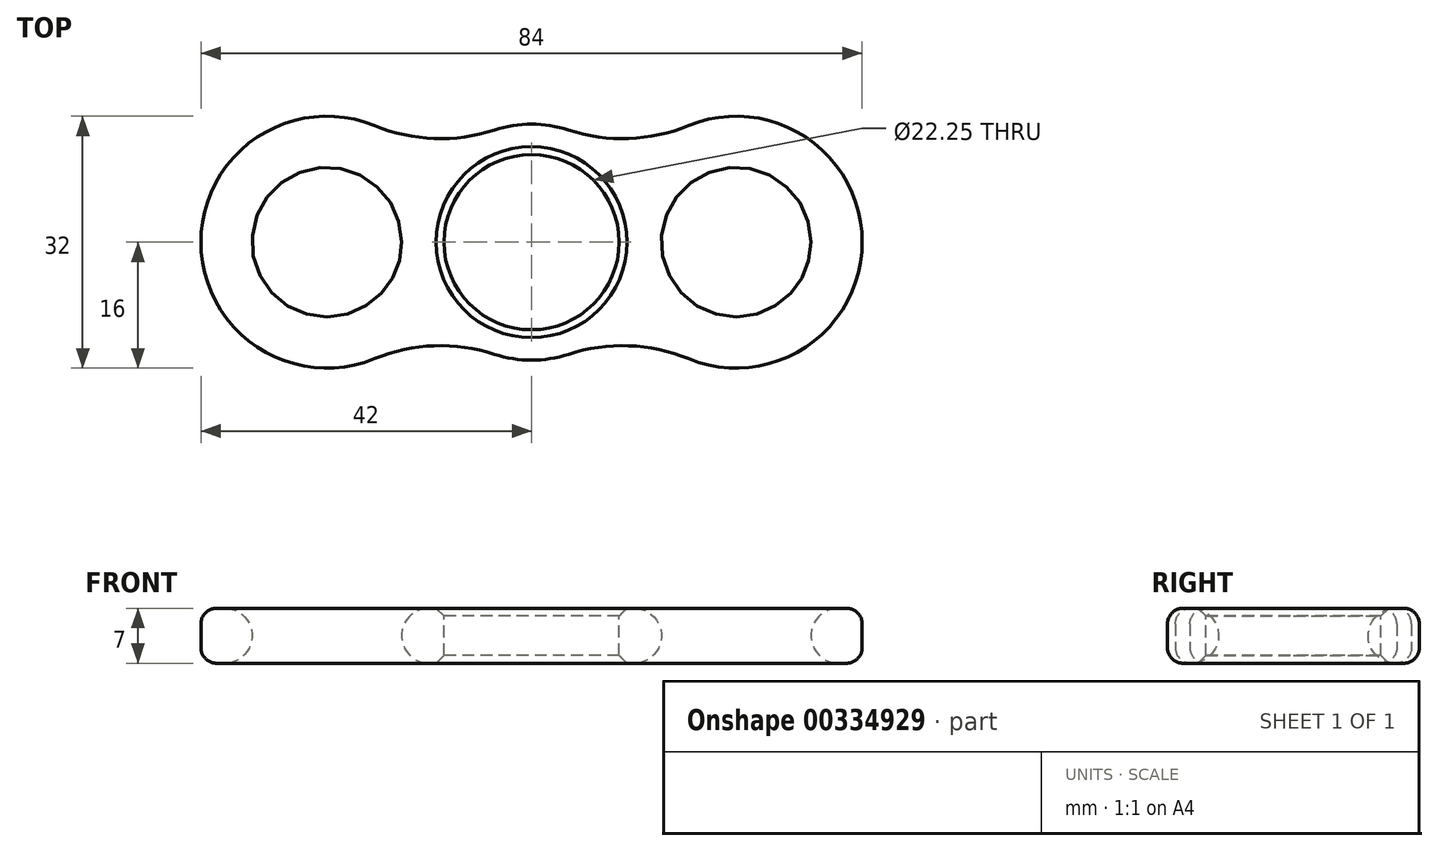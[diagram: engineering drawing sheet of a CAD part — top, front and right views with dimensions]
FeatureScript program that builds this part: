
annotation { "Feature Type Name" : "Feature", "Feature Type Description" : "" }
export const myFeature = defineFeature(function(context is Context, id is Id, definition is map)
    precondition{}
    {
        {
            var Q0;
            Q0=qCreatedBy(makeId("Top.planeOp"),FACE);
            var sketch = newSketch(context, id + "F0", { "sketchPlane" : qUnion([Q0])});
            skArc(sketch, "E0", {"start": v(-4.69, -14.25) * mm, "mid": v(0, -15) * mm, "end": v(4.69, -14.25) * mm});
            skArc(sketch, "E1", {"start": v(-19.92, 14.8) * mm, "mid": v(-40.05, 7.66) * mm, "end": v(-35.14, -13.13) * mm});
            skArc(sketch, "E2", {"start": v(19.92, -14.8) * mm, "mid": v(27.74, -15.9) * mm, "end": v(35.14, -13.13) * mm});
            skArc(sketch, "E3", {"start": v(-19.92, 14.8) * mm, "mid": v(-12.35, 13.16) * mm, "end": v(-4.69, 14.25) * mm});
            skArc(sketch, "E4", {"start": v(-4.69, -14.25) * mm, "mid": v(-12.35, -13.16) * mm, "end": v(-19.92, -14.8) * mm});
            skArc(sketch, "E5", {"start": v(4.69, 14.25) * mm, "mid": v(12.35, 13.16) * mm, "end": v(19.92, 14.8) * mm});
            skArc(sketch, "E6", {"start": v(19.92, -14.8) * mm, "mid": v(12.35, -13.16) * mm, "end": v(4.69, -14.25) * mm});
            skArc(sketch, "E7.trimOffspring", {"start": v(4.69, 14.25) * mm, "mid": v(0, 15) * mm, "end": v(-4.69, 14.25) * mm});
            skArc(sketch, "E8.trimOffspring", {"start": v(-35.14, -13.13) * mm, "mid": v(-27.74, -15.9) * mm, "end": v(-19.92, -14.8) * mm});
            skArc(sketch, "E9.trimOffspring", {"start": v(35.14, -13.13) * mm, "mid": v(40.05, 7.66) * mm, "end": v(19.92, 14.8) * mm});
            skSolve(sketch);
        }
        {
            var Q0;
            Q0=qSketchRegion(id+"F0",true);
            extrude(context, id + "F1", {"entities" : qUnion([Q0]), "depth" : 7 * mm});
        }
        {
            var Q0;
            Q0=makeQuery(id+"F1.opExtrude","CAP_FACE",FACE,{"disambiguationData":[OSD([sQuery(id+"F0.wireOp",EDGE,"E0"),sQuery(id+"F0.wireOp",EDGE,"E1"),sQuery(id+"F0.wireOp",EDGE,"E2"),sQuery(id+"F0.wireOp",EDGE,"E3"),sQuery(id+"F0.wireOp",EDGE,"E4"),sQuery(id+"F0.wireOp",EDGE,"E5"),sQuery(id+"F0.wireOp",EDGE,"E6"),sQuery(id+"F0.wireOp",EDGE,"E7.trimOffspring")])],"isStart":false});
            var sketch = newSketch(context, id + "F2", { "sketchPlane" : qUnion([Q0])});
            skCircle(sketch, "E10", {"center": v(0, 0) * mm, "radius": 11.12 * mm});
            skPoint(sketch, "E10.perimeterSnap0", {"position": v(0, 15) * mm});
            skPoint(sketch, "E10.perimeterSnap1", {"position": v(-12.35, 13.16) * mm});
            skSolve(sketch);
        }
        {
            var Q0;
            Q0=qSketchRegion(id+"F2",true);
            extrude(context, id + "F3", {"entities" : qUnion([Q0]), "operationType" : NewBodyOperationType.REMOVE, "endBound" : BoundingType.THROUGH_ALL, "oppositeDirection" : true, "depth" : 25 * mm});
        }
        {
            var Q0;
            Q0=makeQuery(id+"F1.opExtrude","SWEPT_FACE",FACE,{"disambiguationData":[OSD([sQuery(id+"F0.wireOp",EDGE,"E1"),sQuery(id+"F0.wireOp",EDGE,"E8.trimOffspring")])]});
            var Q1;
            Q1=makeQuery(id+"F1.opExtrude","SWEPT_FACE",FACE,{"disambiguationData":[OSD([sQuery(id+"F0.wireOp",EDGE,"E4")])]});
            var Q2;
            Q2=makeQuery(id+"F1.opExtrude","SWEPT_FACE",FACE,{"disambiguationData":[OSD([sQuery(id+"F0.wireOp",EDGE,"E0")])]});
            var Q3;
            Q3=makeQuery(id+"F1.opExtrude","SWEPT_FACE",FACE,{"disambiguationData":[OSD([sQuery(id+"F0.wireOp",EDGE,"E6")])]});
            var Q4;
            Q4=makeQuery(id+"F1.opExtrude","SWEPT_FACE",FACE,{"disambiguationData":[OSD([sQuery(id+"F0.wireOp",EDGE,"E2"),sQuery(id+"F0.wireOp",EDGE,"E9.trimOffspring")])]});
            var Q5;
            Q5=makeQuery(id+"F1.opExtrude","SWEPT_FACE",FACE,{"disambiguationData":[OSD([sQuery(id+"F0.wireOp",EDGE,"E5")])]});
            var Q6;
            Q6=makeQuery(id+"F1.opExtrude","SWEPT_FACE",FACE,{"disambiguationData":[OSD([sQuery(id+"F0.wireOp",EDGE,"E7.trimOffspring")])]});
            var Q7;
            Q7=makeQuery(id+"F1.opExtrude","SWEPT_FACE",FACE,{"disambiguationData":[OSD([sQuery(id+"F0.wireOp",EDGE,"E3")])]});
            fillet(context, id + "F4", {"entities" : qUnion([Q0, Q1, Q2, Q3, Q4, Q5, Q6, Q7]), "radius" : 2 * mm, "tangentPropagation" : true, "allowEdgeOverflow" : false});
        }
        {
            var Q0;
            Q0=makeQuery(id+"F1.opExtrude","CAP_FACE",FACE,{"disambiguationData":[OSD([sQuery(id+"F0.wireOp",EDGE,"E0"),sQuery(id+"F0.wireOp",EDGE,"E1"),sQuery(id+"F0.wireOp",EDGE,"E2"),sQuery(id+"F0.wireOp",EDGE,"E3"),sQuery(id+"F0.wireOp",EDGE,"E4"),sQuery(id+"F0.wireOp",EDGE,"E5"),sQuery(id+"F0.wireOp",EDGE,"E6"),sQuery(id+"F0.wireOp",EDGE,"E7.trimOffspring"),sQuery(id+"F0.wireOp",EDGE,"E8.trimOffspring"),sQuery(id+"F0.wireOp",EDGE,"E9.trimOffspring")])],"isStart":false});
            var sketch = newSketch(context, id + "F5", { "sketchPlane" : qUnion([Q0])});
            skCircle(sketch, "E11", {"center": v(-26, 0) * mm, "radius": 9.5 * mm});
            skCircle(sketch, "E12", {"center": v(26, 0) * mm, "radius": 9.5 * mm});
            skSolve(sketch);
        }
        {
            var Q0;
            Q0 = qSketchRegion(id + "F5", true);
            extrude(context, id + "F6", {"entities" : qUnion([Q0]), "operationType" : NewBodyOperationType.REMOVE, "endBound" : BoundingType.THROUGH_ALL, "oppositeDirection" : true, "depth" : 1 * mm});
        }
        {
            var Q0;
            Q0=makeQuery(id+"F6.boolean.opBoolean","COPY",FACE,{"derivedFrom":makeQuery(id+"F6.opExtrude","SWEPT_FACE",FACE,{"disambiguationData":[OSD([sQuery(id+"F5.wireOp",EDGE,"E11")])]})});
            var Q1;
            Q1=makeQuery(id+"F6.boolean.opBoolean","COPY",FACE,{"derivedFrom":makeQuery(id+"F6.opExtrude","SWEPT_FACE",FACE,{"disambiguationData":[OSD([sQuery(id+"F5.wireOp",EDGE,"E12")])]})});
            fillet(context, id + "F7", {"entities" : qUnion([Q0, Q1]), "radius" : 3.5 * mm, "tangentPropagation" : true, "allowEdgeOverflow" : false});
        }
        {
            var Q0;
            Q0=makeQuery(id+"F3.boolean.opBoolean","COPY",FACE,{"derivedFrom":makeQuery(id+"F3.opExtrude","SWEPT_FACE",FACE,{"disambiguationData":[OSD([sQuery(id+"F2.wireOp",EDGE,"E10")])]})});
            chamfer(context, id + "F8", {"entities" : qUnion([Q0]), "width" : 1 * mm, "tangentPropagation" : true});
        }
    });
